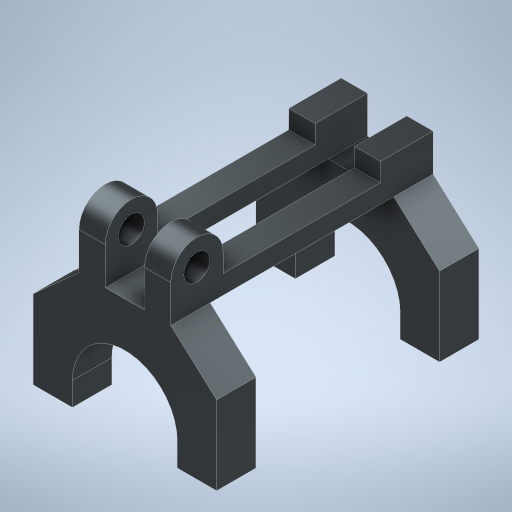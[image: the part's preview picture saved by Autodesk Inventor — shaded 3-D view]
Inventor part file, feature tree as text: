
AUTODESK INVENTOR PART (.ipt)
format: ipt  version: 2024 (Build 280153000, 153)  size: 324,096 bytes
history: native  units: in
note: dims shown in document units (in); Inventor stores cm internally (conversion verified against a paired STEP export)
features: extrude x2, other x2, fillet x1
ambient origin geometry x8: Origin, YZ Plane, XZ Plane, XY Plane, X Axis, Y Axis, Z Axis, Center Point
bodies: Solid1 (feature_tree)
feature tree (5):
  extrude  "front profile Extrusion"  Depth=3.5in
  extrude  "side profile extrusion"  Depth=4.0in
  fillet  "Front Fillet"  Radius=0.875in
  other  "front profile"
  other  "side profile"
